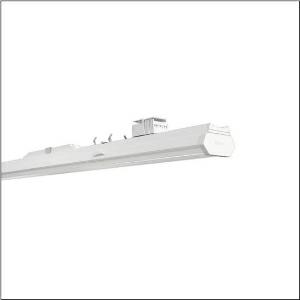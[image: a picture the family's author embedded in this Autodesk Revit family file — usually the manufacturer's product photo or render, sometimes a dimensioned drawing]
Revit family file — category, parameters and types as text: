
# Revit family: licross_r__21_protected_ho_52tp12dn4axm_836c
name_source: partatom
category: Lighting Fixtures
units: mm (PartAtom-declared; Revit-internal decimal feet)

## family parameters
Cut with Voids When Loaded = No
Host = Face
Light Source = No
Part Type = Normal
Room Calculation Point = No
Round Connector Dimension = Use Diameter
Shared = No

## types (1)
- --- (1 x LED, 10000 lm, 56 W, 4000K)
    Apparent Load = 56 VA
    CIE Flux Codes = 70 91 97 98 100
    Color Rendering = 80
    Color Temperature = 4000K
    Default Elevation = 1800 mm
    Description = Licross® 21 Protected HO, luminaire insert, of sheet steel, galvanised, coil coated, white, length: 1.500mm, width: 90mm, height: 103mm, LED rated luminous flux: 10.000lm, light colour: 840, control gear: DALI 2, with plug, 5-pole, with phase selection, mains connection: 220..240V, AC, 50/60Hz, rated input power: 56W, internal wiring halogen-free, primary light control with lens, of plastic, primary optical cover: cover, of PMMA, light emission: direct distribution, primary light characteristic: symmetric, protection rating (complete): IP64, insulation class (complete): insulation class I (protective earthing), certification: CE, ENEC, VDE, UKCA, protection symbol: D if used in an environment with conductive dust loads with corresponding accessories, impact resistance: IK06, permissible ambient temperature for indoor applications: -25..+45°C, corresponds to IFS (International Featured Standards) requirements for safety and quality in the food industry, reducing of maximum allowable ambient temperature of 5°C with ceiling mounting, LABS conformity tested according to VDMA 24364:2018-05, packaging unit: 1 piece
    Height = 92 mm
    Lamp = 1 x LED
    Lamp Light Flux = 10000 lm
    Lamp Power = 56 W
    Lamp count = 1
    Length = 1500 mm
    Luminous efficacy = 179 lm/W
    Manufacturer = Siteco
    ModVariant = No
    Model = 52TP12DN4AXM
    Mounting Place = Ceiling
    Mounting Type = Pendant
    Number of Poles = 1
    OnlyDefault = Yes
    Power Factor = 1
    Product Name = Licross® 21 Protected HO
    Product group = luminaire insert | ceiling pendant
    ProductGroupID = 902
    Protection Class = Protection class I
    Protection Degree = IP 64
    RLX_Detail_Level = 1
    RLX_Emergency_Light_Flux = 0 lm
    RLX_Emergency_Type = 0
    RLX_Emergency_Type_DB = No
    RlxData = <blob elided: 24305 chars, md5=f51ee5e4>
    Socket = socket
    Standby Power = 0 W
    System Light Flux = 10000 lm
    System Power = 56 W
    Type Comments = factory setting: luminous flux: 100 % | dim-lin: 254 | 321 mA
    Type Image = l_1256148.jpg
    URL = http://relux.com
    VarID = @adj_150367
    Voltage = 0 V
    Weight = 0.00 kg
    Width = 88 mm

## geometry (parser evidence)
native form markers: Blend x4, Sweep x10
no freeform markers — native parametric forms only
